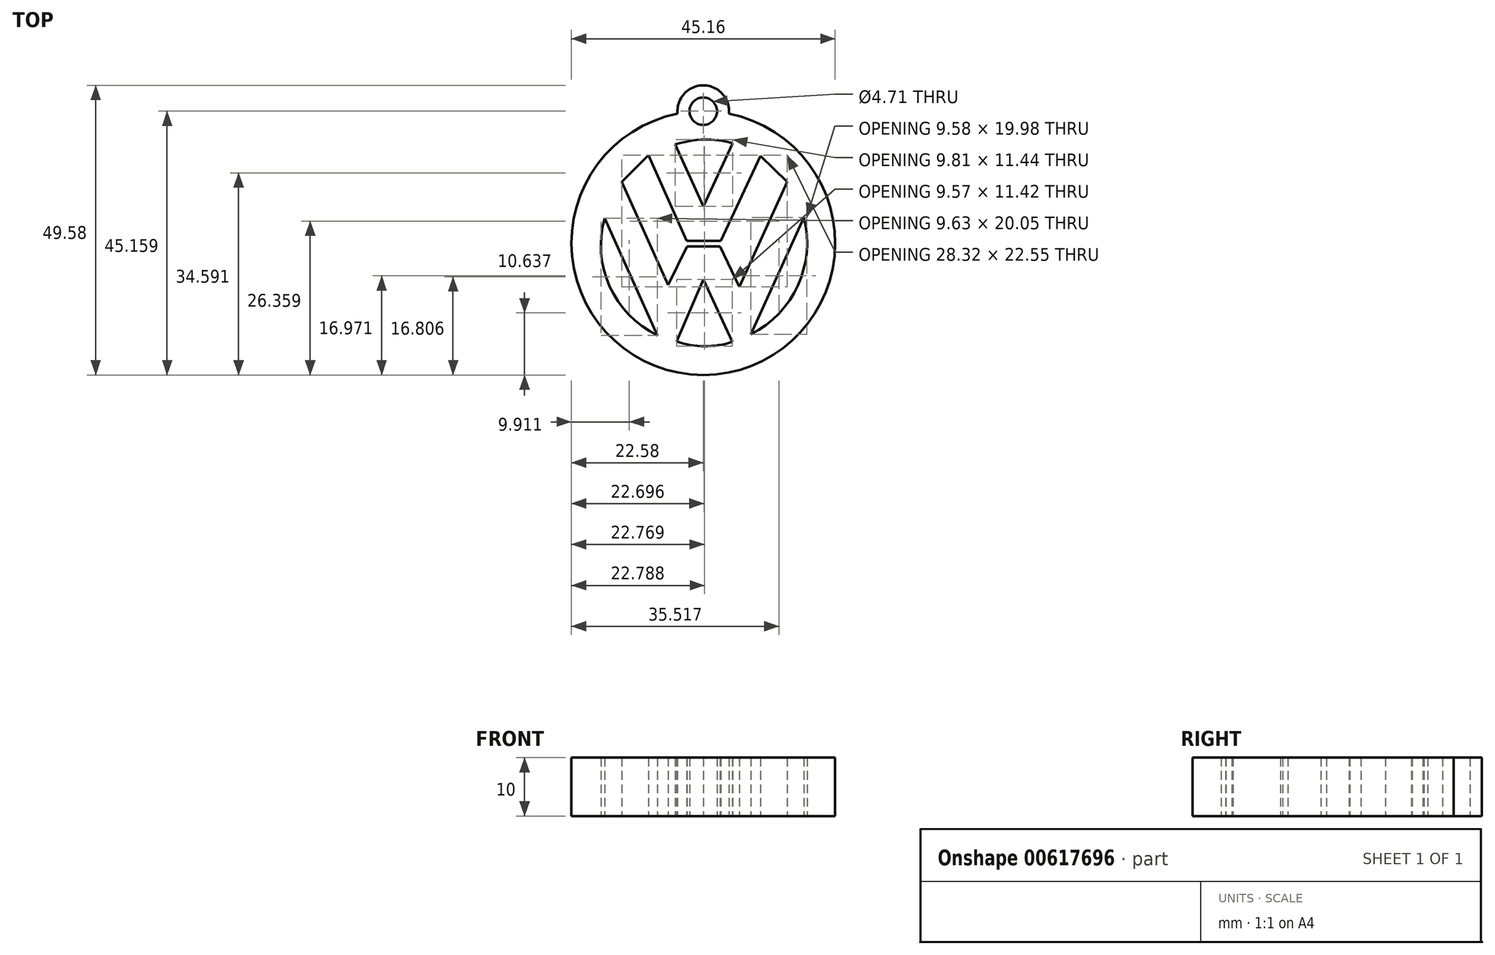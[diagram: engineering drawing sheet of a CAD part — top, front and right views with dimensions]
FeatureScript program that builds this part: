
annotation { "Feature Type Name" : "Feature", "Feature Type Description" : "" }
export const myFeature = defineFeature(function(context is Context, id is Id, definition is map)
    precondition{}
    {
        {
            var Q0;
            Q0=qCreatedBy(makeId("Top.planeOp"),FACE);
            var sketch = newSketch(context, id + "F0", { "sketchPlane" : qUnion([Q0])});
            skArc(sketch, "E0", {"start": v(-4.4, 22.15) * mm, "mid": v(0, -22.58) * mm, "end": v(4.4, 22.15) * mm});
            skLineSegment(sketch, "E1", {"start": v(0, 6.3) * mm, "end": v(-4.79, 16.87) * mm});
            skLineSegment(sketch, "E2", {"start": v(5.02, 17.1) * mm, "end": v(0, 6.3) * mm});
            skLineSegment(sketch, "E3", {"start": v(-6, -7.15) * mm, "end": v(-13.97, 10.46) * mm});
            skLineSegment(sketch, "E4", {"start": v(-2.78, -0.58) * mm, "end": v(2.88, -0.58) * mm});
            skLineSegment(sketch, "E5", {"start": v(2.88, -0.58) * mm, "end": v(6.16, -7.5) * mm});
            skLineSegment(sketch, "E6", {"start": v(6.16, -7.5) * mm, "end": v(14.35, 10.49) * mm});
            skLineSegment(sketch, "E7", {"start": v(14.35, 10.49) * mm, "end": v(9.76, 14.95) * mm});
            skLineSegment(sketch, "E8", {"start": v(9.76, 14.95) * mm, "end": v(3.01, 0.36) * mm});
            skLineSegment(sketch, "E9", {"start": v(-2.83, 0.36) * mm, "end": v(-9.4, 15.05) * mm});
            skLineSegment(sketch, "E10", {"start": v(-9.4, 15.05) * mm, "end": v(-13.97, 10.46) * mm});
            skLineSegment(sketch, "E11", {"start": v(-2.78, -0.58) * mm, "end": v(-6, -7.15) * mm});
            skLineSegment(sketch, "E12", {"start": v(17.24, 4.38) * mm, "end": v(8.15, -15.6) * mm});
            skLineSegment(sketch, "E13", {"start": v(0, -6.23) * mm, "end": v(5, -16.91) * mm});
            skLineSegment(sketch, "E14", {"start": v(0, -6.23) * mm, "end": v(-4.58, -16.85) * mm});
            skLineSegment(sketch, "E15", {"start": v(-16.9, 4.25) * mm, "end": v(-7.85, -15.8) * mm});
            skLineSegment(sketch, "E16", {"start": v(-2.83, 0.36) * mm, "end": v(3.01, 0.36) * mm});
            skArc(sketch, "E17", {"start": v(-16.9, 4.25) * mm, "mid": v(-16.02, -7.42) * mm, "end": v(-7.85, -15.8) * mm});
            skArc(sketch, "E18", {"start": v(-4.58, -16.85) * mm, "mid": v(0.2, -17.65) * mm, "end": v(5, -16.91) * mm});
            skArc(sketch, "E19", {"start": v(5.02, 17.1) * mm, "mid": v(0.1, 17.73) * mm, "end": v(-4.79, 16.87) * mm});
            skArc(sketch, "E20", {"start": v(8.15, -15.6) * mm, "mid": v(16.2, -7.2) * mm, "end": v(17.24, 4.38) * mm});
            skArc(sketch, "E21", {"start": v(4.4, 22.15) * mm, "mid": v(0, 27) * mm, "end": v(-4.4, 22.15) * mm});
            skCircle(sketch, "E22", {"center": v(0, 22.58) * mm, "radius": 2.35 * mm});
            skSolve(sketch);
        }
        {
            var Q0;
            Q0=makeQuery(id+"F0.imprint","IMPRINT",FACE,{"disambiguationData":[TD([[makeQuery(id+"F0.imprint","IMPRINT",EDGE,{"derivedFrom":sQuery(id+"F0.wireOp",EDGE,"E0")}),1.0]])]});
            extrude(context, id + "F1", {"entities" : qUnion([Q0]), "depth" : 10 * mm, "offsetDistance" : 25 * mm});
        }
    });
